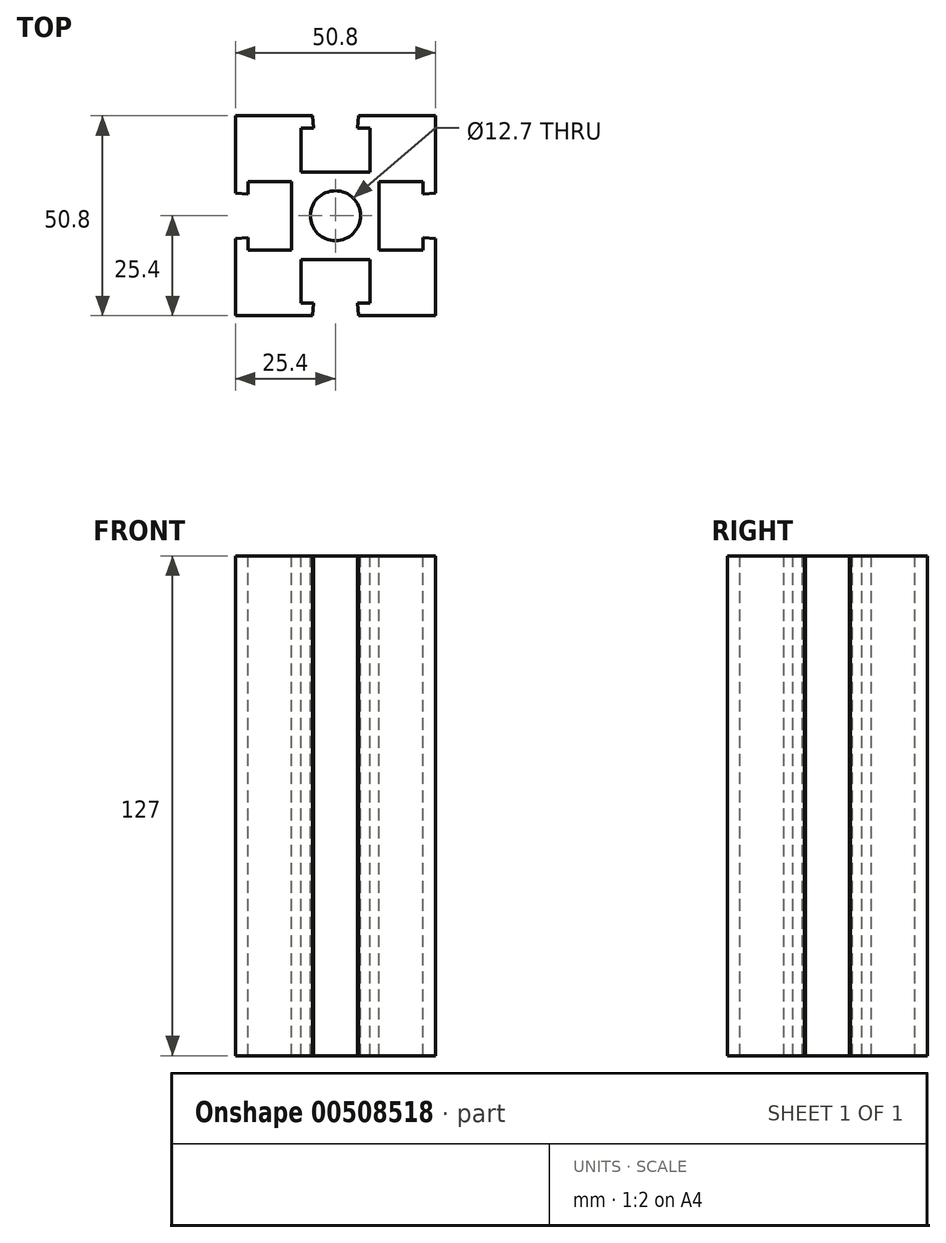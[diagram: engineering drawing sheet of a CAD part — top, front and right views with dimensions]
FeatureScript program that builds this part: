
annotation { "Feature Type Name" : "Feature", "Feature Type Description" : "" }
export const myFeature = defineFeature(function(context is Context, id is Id, definition is map)
    precondition{}
    {
        {
            var Q0;
            Q0=qCreatedBy(makeId("Top.planeOp"),FACE);
            var sketch = newSketch(context, id + "F0", { "sketchPlane" : qUnion([Q0])});
            skLineSegment(sketch, "E0.bottom", {"start": v(0, 0) * mm, "end": v(50.8, 0) * mm});
            skLineSegment(sketch, "E0.top", {"start": v(0, -50.8) * mm, "end": v(50.8, -50.8) * mm});
            skLineSegment(sketch, "E0.left", {"start": v(0, 0) * mm, "end": v(0, -50.8) * mm});
            skLineSegment(sketch, "E0.right", {"start": v(50.8, 0) * mm, "end": v(50.8, -50.8) * mm});
            skSolve(sketch);
        }
        {
            var Q0;
            Q0 = qSketchRegion(id + "F0", true);
            extrude(context, id + "F1", {"entities" : qUnion([Q0]), "depth" : 127 * mm});
        }
        {
            var Q0;
            Q0=makeQuery(id+"F1.opExtrude","CAP_FACE",FACE,{"disambiguationData":[OSD([sQuery(id+"F0.wireOp",EDGE,"E0.bottom"),sQuery(id+"F0.wireOp",EDGE,"E0.top"),sQuery(id+"F0.wireOp",EDGE,"E0.left"),sQuery(id+"F0.wireOp",EDGE,"E0.right")])],"isStart":false});
            var sketch = newSketch(context, id + "F2", { "sketchPlane" : qUnion([Q0])});
            skLineSegment(sketch, "E1", {"start": v(25.4, 0) * mm, "end": v(25.4, -50.8) * mm, "construction": true});
            skLineSegment(sketch, "E2", {"start": v(0, -25.4) * mm, "end": v(50.8, -25.4) * mm, "construction": true});
            skCircle(sketch, "E3", {"center": v(25.4, -25.4) * mm, "radius": 6.35 * mm});
            skLineSegment(sketch, "E4", {"start": v(16.67, -3.18) * mm, "end": v(19.84, -3.18) * mm});
            skLineSegment(sketch, "E5", {"start": v(47.63, -16.67) * mm, "end": v(47.63, -19.84) * mm});
            skLineSegment(sketch, "E6", {"start": v(16.67, -47.63) * mm, "end": v(19.84, -47.63) * mm});
            skLineSegment(sketch, "E7", {"start": v(3.18, -16.67) * mm, "end": v(3.18, -19.84) * mm});
            skLineSegment(sketch, "E8", {"start": v(14.29, -16.67) * mm, "end": v(14.29, -34.13) * mm});
            skLineSegment(sketch, "E9", {"start": v(16.67, -14.29) * mm, "end": v(34.13, -14.29) * mm});
            skLineSegment(sketch, "E10", {"start": v(36.51, -16.67) * mm, "end": v(36.51, -34.13) * mm});
            skLineSegment(sketch, "E11", {"start": v(16.67, -36.51) * mm, "end": v(34.13, -36.51) * mm});
            skLineSegment(sketch, "E12", {"start": v(3.18, -34.13) * mm, "end": v(14.29, -34.13) * mm});
            skLineSegment(sketch, "E13", {"start": v(3.18, -16.67) * mm, "end": v(14.29, -16.67) * mm});
            skLineSegment(sketch, "E14", {"start": v(16.67, -3.18) * mm, "end": v(16.67, -14.29) * mm});
            skLineSegment(sketch, "E15", {"start": v(34.13, -3.17) * mm, "end": v(34.13, -14.29) * mm});
            skLineSegment(sketch, "E16", {"start": v(47.63, -16.67) * mm, "end": v(36.51, -16.67) * mm});
            skLineSegment(sketch, "E17", {"start": v(47.63, -34.13) * mm, "end": v(36.51, -34.13) * mm});
            skLineSegment(sketch, "E18", {"start": v(34.13, -47.63) * mm, "end": v(34.13, -36.51) * mm});
            skLineSegment(sketch, "E19", {"start": v(16.67, -47.63) * mm, "end": v(16.67, -36.51) * mm});
            skLineSegment(sketch, "E20", {"start": v(0, -19.59) * mm, "end": v(3.18, -19.84) * mm});
            skLineSegment(sketch, "E21", {"start": v(3.18, -30.96) * mm, "end": v(0, -31.21) * mm});
            skLineSegment(sketch, "E22", {"start": v(19.84, -47.63) * mm, "end": v(19.59, -50.8) * mm});
            skLineSegment(sketch, "E23", {"start": v(30.96, -47.63) * mm, "end": v(31.21, -50.8) * mm});
            skLineSegment(sketch, "E24", {"start": v(47.63, -30.96) * mm, "end": v(50.8, -31.21) * mm});
            skLineSegment(sketch, "E25", {"start": v(47.63, -19.84) * mm, "end": v(50.8, -19.59) * mm});
            skLineSegment(sketch, "E26", {"start": v(30.96, -3.18) * mm, "end": v(31.21, 0) * mm});
            skLineSegment(sketch, "E27", {"start": v(19.84, -3.18) * mm, "end": v(19.59, 0) * mm});
            skPoint(sketch, "E28", {"position": v(25.4, -3.18) * mm});
            skPoint(sketch, "E29", {"position": v(47.63, -25.4) * mm});
            skPoint(sketch, "E30", {"position": v(25.4, -47.63) * mm});
            skPoint(sketch, "E31", {"position": v(3.18, -25.4) * mm});
            skLineSegment(sketch, "E32.trimOffspring", {"start": v(3.18, -30.96) * mm, "end": v(3.18, -34.13) * mm});
            skLineSegment(sketch, "E33.trimOffspring", {"start": v(30.96, -47.63) * mm, "end": v(34.13, -47.63) * mm});
            skLineSegment(sketch, "E34.trimOffspring", {"start": v(47.63, -30.96) * mm, "end": v(47.63, -34.13) * mm});
            skLineSegment(sketch, "E35.trimOffspring", {"start": v(30.96, -3.17) * mm, "end": v(34.13, -3.17) * mm});
            skSolve(sketch);
        }
        {
            var Q0;
            Q0 = qSketchRegion(id + "F2", true);
            var Q1;
            Q1=makeQuery(id+"F2.imprint","IMPRINT",FACE,{"disambiguationData":[TD([[makeQuery(id+"F2.imprint","IMPRINT",EDGE,{"derivedFrom":sQuery(id+"F2.wireOp",EDGE,"E6")}),1.0]])]});
            var Q2;
            Q2=makeQuery(id+"F2.imprint","IMPRINT",FACE,{"disambiguationData":[TD([[makeQuery(id+"F2.imprint","IMPRINT",EDGE,{"derivedFrom":sQuery(id+"F2.wireOp",EDGE,"E5")}),-1.0]])]});
            var Q3;
            Q3=makeQuery(id+"F2.imprint","IMPRINT",FACE,{"disambiguationData":[TD([[makeQuery(id+"F2.imprint","IMPRINT",EDGE,{"derivedFrom":sQuery(id+"F2.wireOp",EDGE,"E7")}),1.0]])]});
            var Q4;
            Q4=makeQuery(id+"F2.imprint","IMPRINT",FACE,{"disambiguationData":[TD([[makeQuery(id+"F2.imprint","IMPRINT",EDGE,{"derivedFrom":sQuery(id+"F2.wireOp",EDGE,"E4")}),-1.0]])]});
            extrude(context, id + "F3", {"entities" : qUnion([Q0, Q1, Q2, Q3, Q4]), "operationType" : NewBodyOperationType.REMOVE, "oppositeDirection" : true, "depth" : 177.8 * mm, "offsetDistance" : 25.4 * mm});
        }
    });
